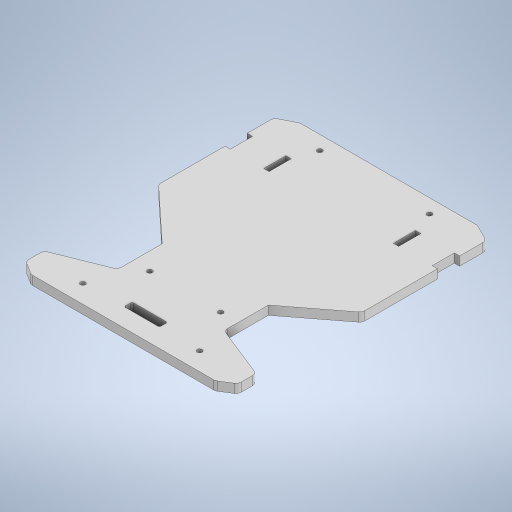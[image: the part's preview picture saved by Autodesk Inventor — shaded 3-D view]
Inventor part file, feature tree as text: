
AUTODESK INVENTOR PART (.ipt)
format: ipt  version: 2023 (Build 270158000, 158)  size: 351,744 bytes
history: native  units: in
note: dims shown in document units (in); Inventor stores cm internally (conversion verified against a paired STEP export)
features: fillet x2, extrude x1, sketch x1
ambient origin geometry x8: Origin, YZ Plane, XZ Plane, XY Plane, X Axis, Y Axis, Z Axis, Center Point
bodies: Solid1 (feature_tree)
feature tree (4):
  extrude  "Extrusion1"  Depth=5.9055in
  fillet  "Fillet1"  Radius=0.7874in
  fillet  "Fillet2"  Radius=0.1181in
  sketch  "Sketch1"  dims[d0=4.7244in d1=5.9055in d2=0.7874in d3=0.1181in d4=0.1181in d5=0.4921in d6=0.7441in d7=0.1181in d8=0.4016in d9=1.2992in d10=2.5984in d11=0.1102in d12=0.1102in d13=1.378in d14=0.7874in d15=1.5748in d16=0.1102in d17=0.1102in d18=2.7559in d19=0.5906in d20=0.3937in d21=0.3937in d22=1.1811in d23=1.1811in d24=0.315in d25=0.315in d26=0.7874in d27=0.1181in d28=0.4921in d29=0.7441in d30=0.1181in d31=0.315in d32=0.1969in d33=0.315in d34=0.1969in d35=0.3937in d36=0.1969in d37=0.3937in d38=0.1969in d39=0.1969in d40=0.0in d41=0.1181in d42=0.0787in d43=0.3937in d44=0.7874in d45=0.1378in d46=0.0394in d47=0.9843in d48=0.9843in d49=1.1417in d50=0.315in d51=1.1417in d52=0.315in d53=0.1102in d54=0.1102in]
